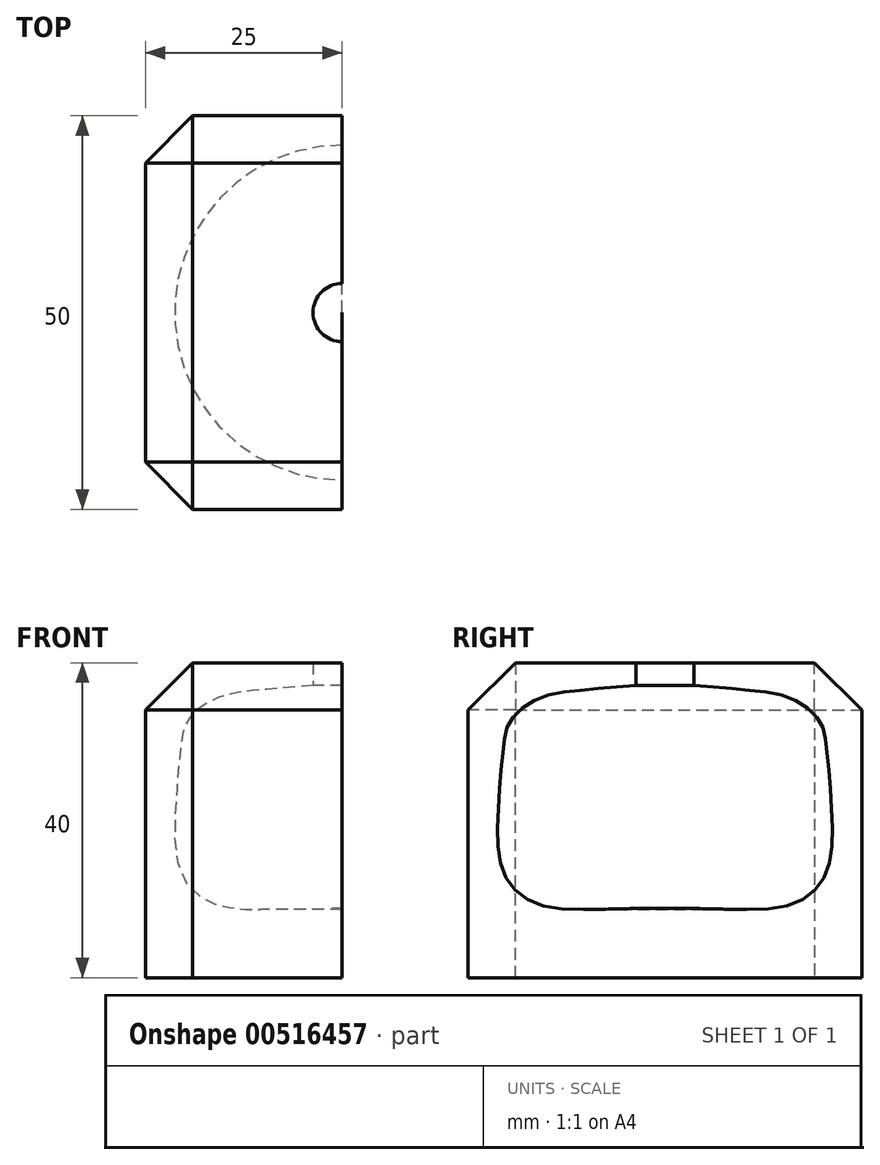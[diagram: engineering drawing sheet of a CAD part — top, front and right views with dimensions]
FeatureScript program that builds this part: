
annotation { "Feature Type Name" : "Feature", "Feature Type Description" : "" }
export const myFeature = defineFeature(function(context is Context, id is Id, definition is map)
    precondition{}
    {
        {
            var Q0;
            Q0=qCreatedBy(makeId("Top.planeOp"),FACE);
            var sketch = newSketch(context, id + "F0", { "sketchPlane" : qUnion([Q0])});
            skLineSegment(sketch, "E0.bottom", {"start": v(25, 25) * mm, "end": v(-25, 25) * mm});
            skLineSegment(sketch, "E0.top", {"start": v(25, -25) * mm, "end": v(-25, -25) * mm});
            skLineSegment(sketch, "E0.left", {"start": v(25, 25) * mm, "end": v(25, -25) * mm});
            skLineSegment(sketch, "E0.right", {"start": v(-25, 25) * mm, "end": v(-25, -25) * mm});
            skPoint(sketch, "E0.middle", {"position": v(0, 0) * mm});
            skSolve(sketch);
        }
        {
            var Q0;
            Q0=makeQuery(id+"F0.imprint","IMPRINT",FACE,{"disambiguationData":[TD([[makeQuery(id+"F0.imprint","IMPRINT",EDGE,{"derivedFrom":sQuery(id+"F0.wireOp",EDGE,"E0.bottom")}),1.0]])]});
            extrude(context, id + "F1", {"entities" : qUnion([Q0]), "depth" : 40 * mm});
        }
        {
            var Q0;
            Q0=makeQuery(id+"F1.opExtrude","CAP_EDGE",EDGE,{"disambiguationData":[OSD([sQuery(id+"F0.wireOp",EDGE,"E0.top")])],"isStart":false});
            var Q1;
            Q1=makeQuery(id+"F1.opExtrude","CAP_EDGE",EDGE,{"disambiguationData":[OSD([sQuery(id+"F0.wireOp",EDGE,"E0.left")])],"isStart":false});
            var Q2;
            Q2=makeQuery(id+"F1.opExtrude","CAP_EDGE",EDGE,{"disambiguationData":[OSD([sQuery(id+"F0.wireOp",EDGE,"E0.bottom")])],"isStart":false});
            var Q3;
            Q3=makeQuery(id+"F1.opExtrude","CAP_EDGE",EDGE,{"disambiguationData":[OSD([sQuery(id+"F0.wireOp",EDGE,"E0.right")])],"isStart":false});
            var Q4;
            Q4=makeQuery(id+"F1.opExtrude","SWEPT_EDGE",EDGE,{"disambiguationData":[OSD([sQuery(id+"F0.wireOp",EDGE,"E0.top"),sQuery(id+"F0.wireOp",EDGE,"E0.left")])]});
            var Q5;
            Q5=makeQuery(id+"F1.opExtrude","SWEPT_EDGE",EDGE,{"disambiguationData":[OSD([sQuery(id+"F0.wireOp",EDGE,"E0.bottom"),sQuery(id+"F0.wireOp",EDGE,"E0.left")])]});
            var Q6;
            Q6=makeQuery(id+"F1.opExtrude","SWEPT_EDGE",EDGE,{"disambiguationData":[OSD([sQuery(id+"F0.wireOp",EDGE,"E0.top"),sQuery(id+"F0.wireOp",EDGE,"E0.right")])]});
            var Q7;
            Q7=makeQuery(id+"F1.opExtrude","SWEPT_EDGE",EDGE,{"disambiguationData":[OSD([sQuery(id+"F0.wireOp",EDGE,"E0.bottom"),sQuery(id+"F0.wireOp",EDGE,"E0.right")])]});
            chamfer(context, id + "F2", {"entities" : qUnion([Q0, Q1, Q2, Q3, Q4, Q5, Q6, Q7]), "width" : 6 * mm, "tangentPropagation" : true});
        }
        {
            var Q0;
            Q0=qCreatedBy(makeId("Right.planeOp"),FACE);
            var sketch = newSketch(context, id + "F3", { "sketchPlane" : qUnion([Q0])});
            skLineSegment(sketch, "E1.bottom", {"start": v(-40.57, 50.74) * mm, "end": v(43.2, 50.74) * mm});
            skLineSegment(sketch, "E1.top", {"start": v(-40.57, 0) * mm, "end": v(43.2, 0) * mm});
            skLineSegment(sketch, "E1.left", {"start": v(-40.57, 50.74) * mm, "end": v(-40.57, 0) * mm});
            skLineSegment(sketch, "E1.right", {"start": v(43.2, 50.74) * mm, "end": v(43.2, 0) * mm});
            skSolve(sketch);
        }
        {
            var Q0;
            Q0 = qSketchRegion(id + "F3", true);
            extrude(context, id + "F4", {"entities" : qUnion([Q0]), "operationType" : NewBodyOperationType.REMOVE, "depth" : 25 * mm, "offsetDistance" : 25 * mm});
        }
        {
            var Q0;
            Q0=makeQuery(id+"F4.boolean.opBoolean","COPY",FACE,{"derivedFrom":makeQuery(id+"F4.opExtrude","CAP_FACE",FACE,{"disambiguationData":[OSD([sQuery(id+"F3.wireOp",EDGE,"E1.bottom"),sQuery(id+"F3.wireOp",EDGE,"E1.top"),sQuery(id+"F3.wireOp",EDGE,"E1.left"),sQuery(id+"F3.wireOp",EDGE,"E1.right")])],"isStart":true})});
            var sketch = newSketch(context, id + "F5", { "sketchPlane" : qUnion([Q0])});
            skFitSpline(sketch, "E2", {"points": [v(0, 8.81) * mm, v(-16.08, 9.32) * mm, v(-20.45, 13.18) * mm, v(-21.2, 20.75) * mm, v(-20.53, 29.23) * mm, v(-19.6, 32.68) * mm, v(-15.91, 35.54) * mm, v(-9.6, 36.63) * mm, v(0, 37.22) * mm], "startDerivative": vector(-125.05, 1.37) * mm, "endDerivative": vector(75.35, -1.1) * mm});
            skLineSegment(sketch, "E3", {"start": v(-3.7, 40) * mm, "end": v(-3.7, 36.59) * mm});
            skLineSegment(sketch, "E4", {"start": v(-3.7, 40) * mm, "end": v(0, 40) * mm});
            skLineSegment(sketch, "E5", {"start": v(0, 40) * mm, "end": v(0, 8.81) * mm});
            skSolve(sketch);
        }
        {
            var Q0;
            Q0 = qSketchRegion(id + "F5", true);
            var Q1;
            Q1=sQuery(id+"F5.wireOp",EDGE,"E5");
            revolve(context, id + "F6", {"operationType" : NewBodyOperationType.REMOVE, "entities" : qUnion([Q0]), "axis" : qUnion([Q1]), "revolveType" : RevolveType.FULL, "oppositeDirection" : true});
        }
    });
